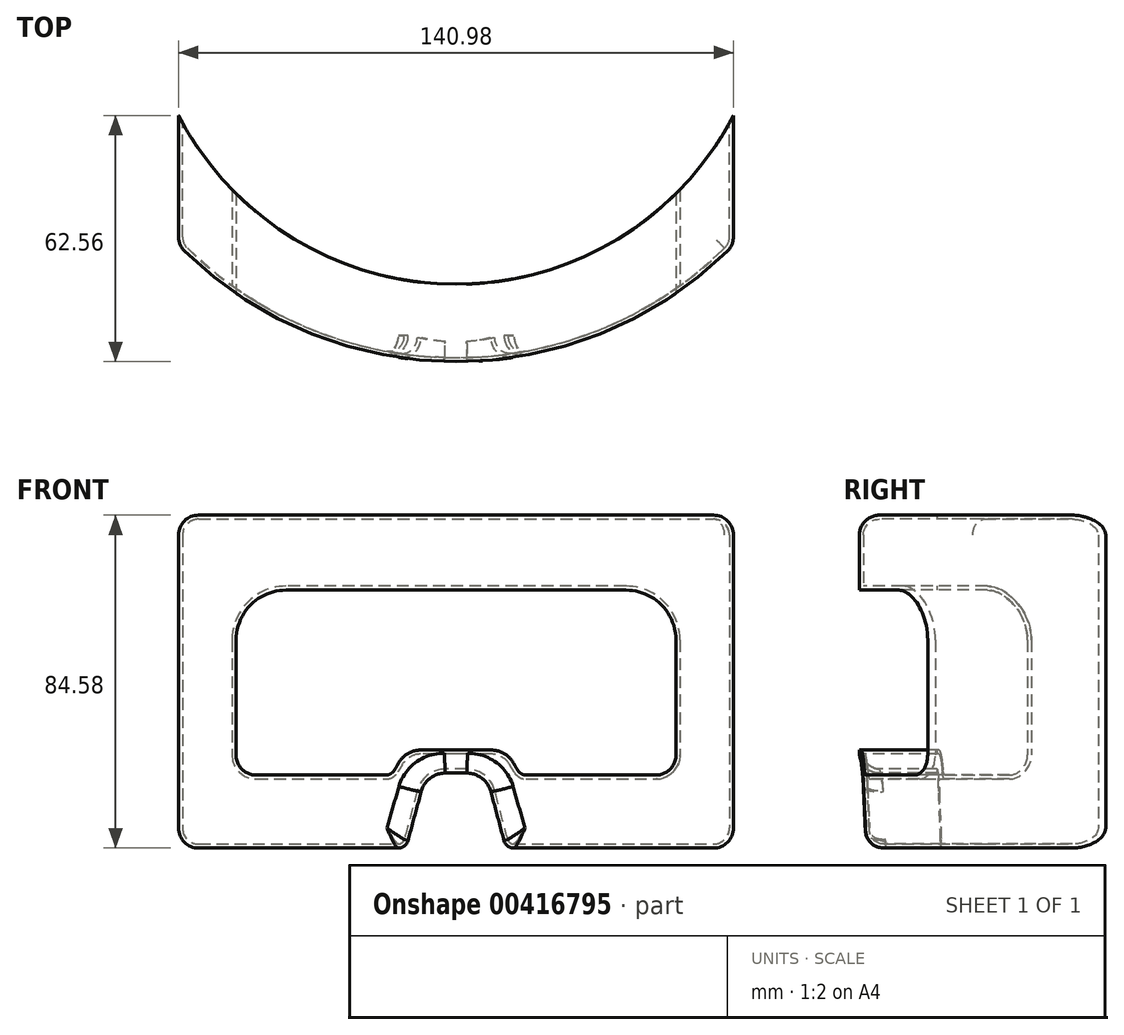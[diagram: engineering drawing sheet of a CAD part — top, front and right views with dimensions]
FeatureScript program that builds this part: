
annotation { "Feature Type Name" : "Feature", "Feature Type Description" : "" }
export const myFeature = defineFeature(function(context is Context, id is Id, definition is map)
    precondition{}
    {
        {
            var Q0;
            Q0=qCreatedBy(makeId("Top.planeOp"),FACE);
            var sketch = newSketch(context, id + "F0", { "sketchPlane" : qUnion([Q0])});
            skArc(sketch, "E0", {"start": v(-70.48, 29.62) * mm, "mid": v(0, 0) * mm, "end": v(70.48, 29.62) * mm});
            skLineSegment(sketch, "E1", {"start": v(0, 0) * mm, "end": v(0, 213.32) * mm, "construction": true});
            skArc(sketch, "E2", {"start": v(-70.48, 78.64) * mm, "mid": v(0, 25.4) * mm, "end": v(70.48, 78.64) * mm});
            skLineSegment(sketch, "E3", {"start": v(-70.48, 78.64) * mm, "end": v(-70.48, 29.62) * mm});
            skLineSegment(sketch, "E4", {"start": v(70.48, 78.64) * mm, "end": v(70.48, 29.62) * mm});
            skSolve(sketch);
        }
        {
            var Q0;
            Q0 = qSketchRegion(id + "F0", true);
            extrude(context, id + "F1", {"entities" : qUnion([Q0]), "depth" : 84.58 * mm, "offsetDistance" : 25.4 * mm});
        }
        {
            var Q0;
            Q0=makeQuery(id+"F1.opExtrude","CAP_EDGE",EDGE,{"disambiguationData":[OSD([sQuery(id+"F0.wireOp",EDGE,"E0")])],"isStart":false});
            var Q1;
            Q1=makeQuery(id+"F1.opExtrude","CAP_EDGE",EDGE,{"disambiguationData":[OSD([sQuery(id+"F0.wireOp",EDGE,"E3")])],"isStart":false});
            var Q2;
            Q2=makeQuery(id+"F1.opExtrude","CAP_EDGE",EDGE,{"disambiguationData":[OSD([sQuery(id+"F0.wireOp",EDGE,"E2")])],"isStart":false});
            var Q3;
            Q3=makeQuery(id+"F1.opExtrude","SWEPT_EDGE",EDGE,{"disambiguationData":[OSD([sQuery(id+"F0.wireOp",EDGE,"E0"),sQuery(id+"F0.wireOp",EDGE,"E4")])]});
            var Q4;
            Q4=makeQuery(id+"F1.opExtrude","SWEPT_EDGE",EDGE,{"disambiguationData":[OSD([sQuery(id+"F0.wireOp",EDGE,"E0"),sQuery(id+"F0.wireOp",EDGE,"E3")])]});
            var Q5;
            Q5=makeQuery(id+"F1.opExtrude","CAP_EDGE",EDGE,{"disambiguationData":[OSD([sQuery(id+"F0.wireOp",EDGE,"E4")])],"isStart":false});
            fillet(context, id + "F2", {"entities" : qUnion([Q0, Q1, Q2, Q3, Q4, Q5]), "radius" : 5.08 * mm, "tangentPropagation" : true, "allowEdgeOverflow" : false});
        }
        {
            var Q0;
            Q0=qCreatedBy(makeId("Front.planeOp"),FACE);
            var sketch = newSketch(context, id + "F3", { "sketchPlane" : qUnion([Q0])});
            skLineSegment(sketch, "E5", {"start": v(12.7, 0) * mm, "end": v(-12.7, 0) * mm});
            skLineSegment(sketch, "E6", {"start": v(-12.2, 1.88) * mm, "end": v(-8.86, 14.34) * mm});
            skLineSegment(sketch, "E7", {"start": v(8.86, 14.34) * mm, "end": v(12.2, 1.88) * mm});
            skLineSegment(sketch, "E8", {"start": v(14.65, 0) * mm, "end": v(22.86, 0) * mm});
            skLineSegment(sketch, "E9", {"start": v(-14.65, 0) * mm, "end": v(-22.86, 0) * mm});
            skPoint(sketch, "E10.visualSharp", {"position": v(12.7, 0) * mm});
            skArc(sketch, "E10.filletArc", {"start": v(12.2, 1.88) * mm, "mid": v(13.1, 0.52) * mm, "end": v(14.65, 0) * mm});
            skPoint(sketch, "E11.visualSharp", {"position": v(-12.7, 0) * mm});
            skArc(sketch, "E11.filletArc", {"start": v(-14.65, 0) * mm, "mid": v(-13.1, 0.52) * mm, "end": v(-12.2, 1.88) * mm});
            skLineSegment(sketch, "E12", {"start": v(-14.65, 0) * mm, "end": v(-12.7, 0) * mm});
            skLineSegment(sketch, "E13", {"start": v(12.7, 0) * mm, "end": v(14.65, 0) * mm});
            skLineSegment(sketch, "E14", {"start": v(-2.72, 19.05) * mm, "end": v(2.72, 19.05) * mm});
            skPoint(sketch, "E15.visualSharp", {"position": v(-7.6, 19.05) * mm});
            skArc(sketch, "E15.filletArc", {"start": v(-2.72, 19.05) * mm, "mid": v(-6.59, 17.74) * mm, "end": v(-8.86, 14.34) * mm});
            skPoint(sketch, "E16.visualSharp", {"position": v(7.6, 19.05) * mm});
            skArc(sketch, "E16.filletArc", {"start": v(8.86, 14.34) * mm, "mid": v(6.59, 17.74) * mm, "end": v(2.72, 19.05) * mm});
            skSolve(sketch);
        }
        {
            var Q0;
            Q0 = qSketchRegion(id + "F3", true);
            extrude(context, id + "F4", {"entities" : qUnion([Q0]), "operationType" : NewBodyOperationType.REMOVE, "endBound" : BoundingType.THROUGH_ALL, "oppositeDirection" : true, "depth" : 25.4 * mm, "offsetDistance" : 25.4 * mm});
        }
        {
            var Q0;
            {var subQ0=sQuery(id+"F0.wireOp",EDGE,"E0");Q0=makeQuery(id+"F4.boolean.opBoolean","SPLIT",EDGE,{"disambiguationData":[TD([makeQuery(id+"F4.opExtrude","SWEPT_FACE",FACE,{"disambiguationData":[OSD([sQuery(id+"F3.wireOp",EDGE,"E7")])]})])],"derivedFrom":makeQuery(id+"F1.opExtrude","CAP_EDGE",EDGE,{"disambiguationData":[OSD([subQ0])],"isStart":true})});}
            var Q1;
            {var subQ1=sQuery(id+"F0.wireOp",EDGE,"E2");Q1=makeQuery(id+"F4.boolean.opBoolean","SPLIT",EDGE,{"disambiguationData":[TD([makeQuery(id+"F4.opExtrude","SWEPT_FACE",FACE,{"disambiguationData":[OSD([sQuery(id+"F3.wireOp",EDGE,"E7")])]})])],"derivedFrom":makeQuery(id+"F1.opExtrude","CAP_EDGE",EDGE,{"disambiguationData":[OSD([subQ1])],"isStart":true})});}
            var Q2;
            Q2=makeQuery(id+"F4.boolean.opBoolean","INTERSECT",EDGE,{"derivedFrom":[makeQuery(id+"F1.opExtrude","SWEPT_FACE",FACE,{"disambiguationData":[OSD([sQuery(id+"F0.wireOp",EDGE,"E0")])]}),makeQuery(id+"F4.opExtrude","SWEPT_FACE",FACE,{"disambiguationData":[OSD([sQuery(id+"F3.wireOp",EDGE,"E7")])]})]});
            var Q3;
            Q3=makeQuery(id+"F4.boolean.opBoolean","INTERSECT",EDGE,{"derivedFrom":[makeQuery(id+"F1.opExtrude","SWEPT_FACE",FACE,{"disambiguationData":[OSD([sQuery(id+"F0.wireOp",EDGE,"E2")])]}),makeQuery(id+"F4.opExtrude","SWEPT_FACE",FACE,{"disambiguationData":[OSD([sQuery(id+"F3.wireOp",EDGE,"E6")])]})]});
            var Q4;
            {var subQ0=sQuery(id+"F0.wireOp",EDGE,"E0");Q4=makeQuery(id+"F4.boolean.opBoolean","SPLIT",EDGE,{"disambiguationData":[TD([makeQuery(id+"F4.opExtrude","SWEPT_FACE",FACE,{"disambiguationData":[OSD([sQuery(id+"F3.wireOp",EDGE,"E6")])]})])],"derivedFrom":makeQuery(id+"F1.opExtrude","CAP_EDGE",EDGE,{"disambiguationData":[OSD([subQ0])],"isStart":true})});}
            fillet(context, id + "F5", {"entities" : qUnion([Q0, Q1, Q2, Q3, Q4]), "radius" : 5.08 * mm, "tangentPropagation" : true, "allowEdgeOverflow" : false});
        }
        {
            var Q0;
            Q0=qCreatedBy(makeId("Front.planeOp"),FACE);
            var sketch = newSketch(context, id + "F6", { "sketchPlane" : qUnion([Q0])});
            skLineSegment(sketch, "E17.bottom", {"start": v(-43.18, 65.53) * mm, "end": v(43.18, 65.53) * mm});
            skLineSegment(sketch, "E17.left", {"start": v(-55.88, 52.83) * mm, "end": v(-55.88, 23.62) * mm});
            skLineSegment(sketch, "E17.right", {"start": v(55.88, 52.83) * mm, "end": v(55.88, 23.62) * mm});
            skPoint(sketch, "E18.visualSharp", {"position": v(-55.88, 65.53) * mm});
            skArc(sketch, "E18.filletArc", {"start": v(-43.18, 65.53) * mm, "mid": v(-52.16, 61.81) * mm, "end": v(-55.88, 52.83) * mm});
            skPoint(sketch, "E19.visualSharp", {"position": v(-55.88, 18.54) * mm});
            skArc(sketch, "E19.filletArc", {"start": v(-55.88, 23.62) * mm, "mid": v(-54.4, 20.03) * mm, "end": v(-50.8, 18.54) * mm});
            skPoint(sketch, "E20.visualSharp", {"position": v(55.88, 18.54) * mm});
            skArc(sketch, "E20.filletArc", {"start": v(50.8, 18.54) * mm, "mid": v(54.4, 20.03) * mm, "end": v(55.88, 23.62) * mm});
            skPoint(sketch, "E21.visualSharp", {"position": v(55.88, 65.53) * mm});
            skArc(sketch, "E21.filletArc", {"start": v(55.88, 52.83) * mm, "mid": v(52.16, 61.81) * mm, "end": v(43.18, 65.53) * mm});
            skLineSegment(sketch, "E22", {"start": v(50.8, 18.54) * mm, "end": v(17.83, 18.54) * mm});
            skLineSegment(sketch, "E23", {"start": v(-17.83, 18.54) * mm, "end": v(-50.8, 18.54) * mm});
            skLineSegment(sketch, "E24", {"start": v(-15.63, 19.81) * mm, "end": v(-14.53, 21.72) * mm});
            skLineSegment(sketch, "E25", {"start": v(-9.03, 24.9) * mm, "end": v(9.03, 24.9) * mm});
            skLineSegment(sketch, "E26", {"start": v(14.53, 21.72) * mm, "end": v(15.63, 19.81) * mm});
            skLineSegment(sketch, "E27", {"start": v(0, 0) * mm, "end": v(0, 107.87) * mm, "construction": true});
            skPoint(sketch, "E28.visualSharp", {"position": v(-12.7, 24.9) * mm});
            skArc(sketch, "E28.filletArc", {"start": v(-9.03, 24.9) * mm, "mid": v(-12.2, 24.04) * mm, "end": v(-14.53, 21.72) * mm});
            skPoint(sketch, "E29.visualSharp", {"position": v(12.7, 24.9) * mm});
            skArc(sketch, "E29.filletArc", {"start": v(14.53, 21.72) * mm, "mid": v(12.2, 24.04) * mm, "end": v(9.03, 24.9) * mm});
            skPoint(sketch, "E30.visualSharp", {"position": v(16.37, 18.54) * mm});
            skArc(sketch, "E30.filletArc", {"start": v(15.63, 19.81) * mm, "mid": v(16.56, 18.88) * mm, "end": v(17.83, 18.54) * mm});
            skPoint(sketch, "E31.visualSharp", {"position": v(-16.37, 18.54) * mm});
            skArc(sketch, "E31.filletArc", {"start": v(-17.83, 18.54) * mm, "mid": v(-16.56, 18.88) * mm, "end": v(-15.63, 19.81) * mm});
            skSolve(sketch);
        }
        {
            var Q0;
            Q0 = qSketchRegion(id + "F6", true);
            extrude(context, id + "F7", {"entities" : qUnion([Q0]), "operationType" : NewBodyOperationType.REMOVE, "oppositeDirection" : true, "depth" : 76.2 * mm});
        }
        {
            var Q0;
            Q0=makeQuery(id+"F7.boolean.opBoolean","INTERSECT",EDGE,{"derivedFrom":[makeQuery(id+"F1.opExtrude","SWEPT_FACE",FACE,{"disambiguationData":[OSD([sQuery(id+"F0.wireOp",EDGE,"E0")])]}),makeQuery(id+"F7.opExtrude","SWEPT_FACE",FACE,{"disambiguationData":[OSD([sQuery(id+"F6.wireOp",EDGE,"E17.top")])]})]});
            var Q1;
            {var subQ0=sQuery(id+"F0.wireOp",EDGE,"E4");var subQ1=sQuery(id+"F0.wireOp",EDGE,"E2");Q1=makeQuery(id+"F7.boolean.opBoolean","INTERSECT",EDGE,{"derivedFrom":[makeQuery(id+"F2.opFillet","BLEND_FACE",FACE,{"disambiguationData":[OSD([subQ1,subQ0]),TDD([makeQuery(id+"F1.opExtrude","SWEPT_EDGE",EDGE,{"disambiguationData":[OSD([subQ1,subQ0])]})])]}),makeQuery(id+"F7.opExtrude","SWEPT_FACE",FACE,{"disambiguationData":[OSD([sQuery(id+"F6.wireOp",EDGE,"E17.right")])]})]});}
            var Q2;
            Q2=makeQuery(id+"F7.boolean.opBoolean","INTERSECT",EDGE,{"derivedFrom":[makeQuery(id+"F1.opExtrude","SWEPT_FACE",FACE,{"disambiguationData":[OSD([sQuery(id+"F0.wireOp",EDGE,"E2")])]}),makeQuery(id+"F7.opExtrude","SWEPT_FACE",FACE,{"disambiguationData":[OSD([sQuery(id+"F6.wireOp",EDGE,"E17.bottom")])]})]});
            fillet(context, id + "F8", {"entities" : qUnion([Q0, Q1, Q2]), "radius" : 0.64 * mm, "tangentPropagation" : true, "allowEdgeOverflow" : false});
        }
        {
            var Q0;
            Q0=qCreatedBy(makeId("Front.planeOp"),FACE);
            var sketch = newSketch(context, id + "F9", { "sketchPlane" : qUnion([Q0])});
            skLineSegment(sketch, "E32.bottom", {"start": v(-49.53, 65.53) * mm, "end": v(49.53, 65.53) * mm});
            skLineSegment(sketch, "E32.top", {"start": v(-49.53, 14.73) * mm, "end": v(49.53, 14.73) * mm});
            skLineSegment(sketch, "E32.left", {"start": v(-55.88, 59.18) * mm, "end": v(-55.88, 21.08) * mm});
            skLineSegment(sketch, "E32.right", {"start": v(55.88, 59.18) * mm, "end": v(55.88, 21.08) * mm});
            skPoint(sketch, "E33.visualSharp", {"position": v(-55.88, 65.53) * mm});
            skArc(sketch, "E33.filletArc", {"start": v(-49.53, 65.53) * mm, "mid": v(-54.02, 63.67) * mm, "end": v(-55.88, 59.18) * mm});
            skPoint(sketch, "E34.visualSharp", {"position": v(-55.88, 14.73) * mm});
            skArc(sketch, "E34.filletArc", {"start": v(-55.88, 21.08) * mm, "mid": v(-54.02, 16.6) * mm, "end": v(-49.53, 14.73) * mm});
            skPoint(sketch, "E35.visualSharp", {"position": v(55.88, 14.73) * mm});
            skArc(sketch, "E35.filletArc", {"start": v(49.53, 14.73) * mm, "mid": v(54.02, 16.6) * mm, "end": v(55.88, 21.08) * mm});
            skPoint(sketch, "E36.visualSharp", {"position": v(55.88, 65.53) * mm});
            skArc(sketch, "E36.filletArc", {"start": v(55.88, 59.18) * mm, "mid": v(54.02, 63.67) * mm, "end": v(49.53, 65.53) * mm});
            skSolve(sketch);
        }
        {
            var Q0;
            Q0=makeQuery(id+"F1.opExtrude","SWEPT_FACE",FACE,{"disambiguationData":[OSD([sQuery(id+"F0.wireOp",EDGE,"E2")])]});
            shell(context, id + "F10", {"entities" : qUnion([Q0]), "thickness" : 1.02 * mm});
        }
        {
            var Q0;
            Q0=qCreatedBy(makeId("Top.planeOp"),FACE);
            var sketch = newSketch(context, id + "F11", { "sketchPlane" : qUnion([Q0])});
            skCircle(sketch, "E37", {"center": v(0, 99.06) * mm, "radius": 79.38 * mm});
            skLineSegment(sketch, "E38", {"start": v(0, -77) * mm, "end": v(0, 229.17) * mm, "construction": true});
            skSolve(sketch);
        }
        {
            var Q0;
            Q0 = qSketchRegion(id + "F11", true);
            extrude(context, id + "F12", {"entities" : qUnion([Q0]), "operationType" : NewBodyOperationType.REMOVE, "endBound" : BoundingType.THROUGH_ALL, "depth" : 76.2 * mm, "offsetDistance" : 25.4 * mm});
        }
    });
